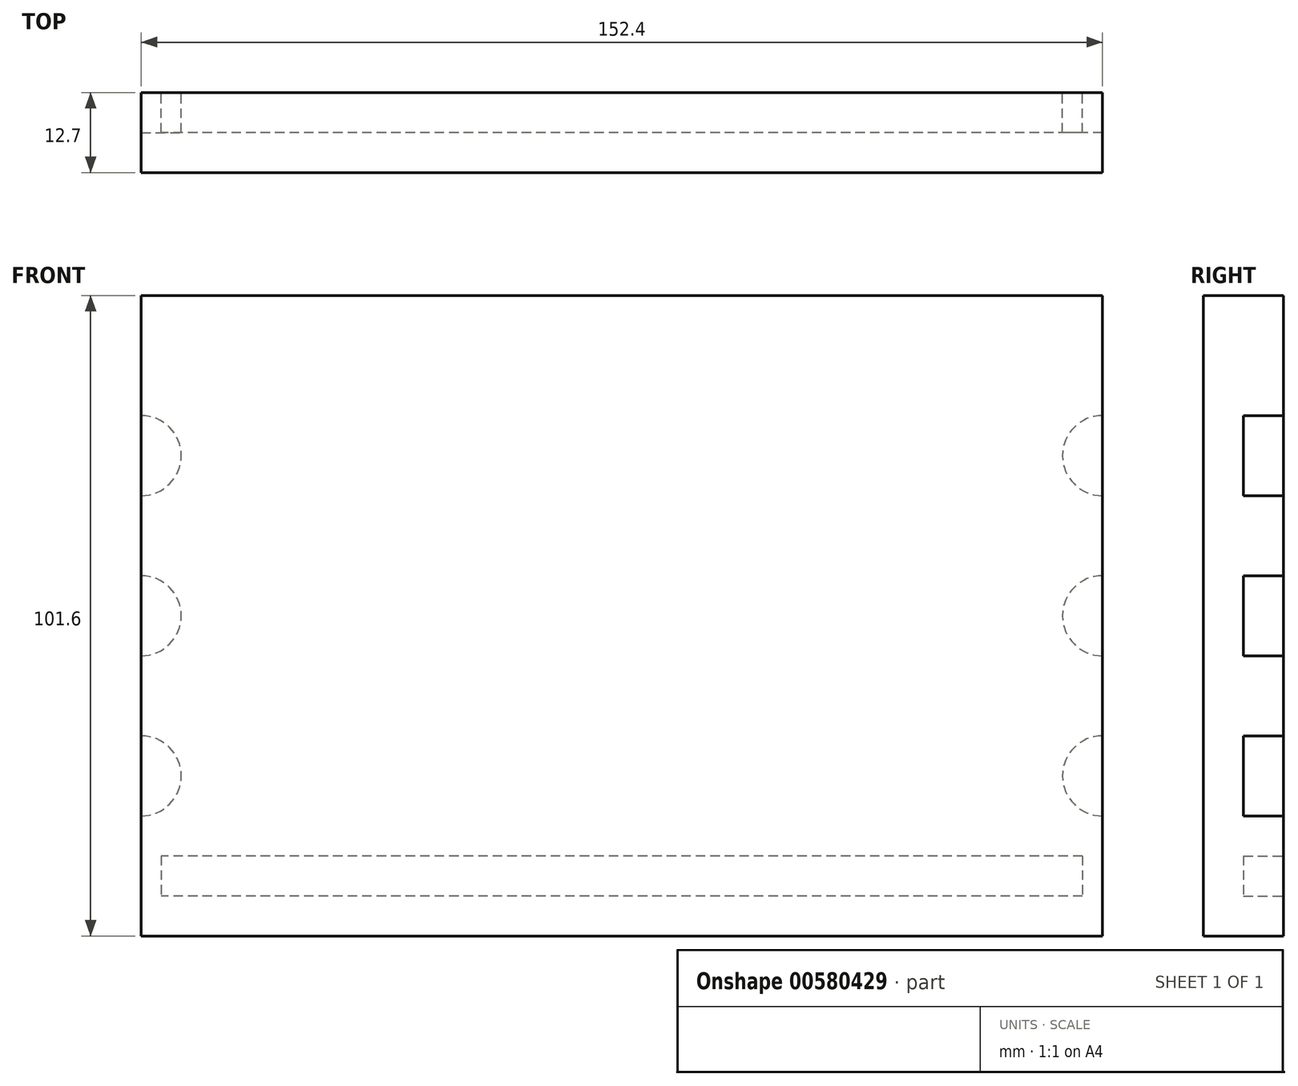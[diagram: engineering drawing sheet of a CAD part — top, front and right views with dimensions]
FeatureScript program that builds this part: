
annotation { "Feature Type Name" : "Feature", "Feature Type Description" : "" }
export const myFeature = defineFeature(function(context is Context, id is Id, definition is map)
    precondition{}
    {
        {
            var Q0;
            Q0=qCreatedBy(makeId("Front.planeOp"),FACE);
            var sketch = newSketch(context, id + "F0", { "sketchPlane" : qUnion([Q0])});
            skLineSegment(sketch, "E0.bottom", {"start": v(76.2, 50.8) * mm, "end": v(-76.2, 50.8) * mm});
            skLineSegment(sketch, "E0.top", {"start": v(76.2, -50.8) * mm, "end": v(-76.2, -50.8) * mm});
            skLineSegment(sketch, "E0.left", {"start": v(76.2, 50.8) * mm, "end": v(76.2, -50.8) * mm});
            skLineSegment(sketch, "E0.right", {"start": v(-76.2, 50.8) * mm, "end": v(-76.2, -50.8) * mm});
            skPoint(sketch, "E0.middle", {"position": v(0, 0) * mm});
            skSolve(sketch);
        }
        {
            var Q0;
            Q0 = qSketchRegion(id + "F0", true);
            var Q1;
            Q1=makeQuery(id+"F0.imprint","IMPRINT",FACE,{"disambiguationData":[TD([[makeQuery(id+"F0.imprint","IMPRINT",EDGE,{"derivedFrom":sQuery(id+"F0.wireOp",EDGE,"E0.bottom")}),1.0]])]});
            extrude(context, id + "F1", {"entities" : qUnion([Q0, Q1]), "depth" : 12.7 * mm, "offsetDistance" : 25.4 * mm});
        }
        {
            var Q0;
            Q0=makeQuery(id+"F1.opExtrude","CAP_FACE",FACE,{"disambiguationData":[OSD([sQuery(id+"F0.wireOp",EDGE,"E0.bottom"),sQuery(id+"F0.wireOp",EDGE,"E0.top"),sQuery(id+"F0.wireOp",EDGE,"E0.left"),sQuery(id+"F0.wireOp",EDGE,"E0.right")])],"isStart":true});
            var sketch = newSketch(context, id + "F2", { "sketchPlane" : qUnion([Q0])});
            skLineSegment(sketch, "E1.bottom", {"start": v(-73.03, -38.1) * mm, "end": v(73.03, -38.1) * mm});
            skLineSegment(sketch, "E1.top", {"start": v(-73.03, -44.45) * mm, "end": v(73.03, -44.45) * mm});
            skLineSegment(sketch, "E1.left", {"start": v(-73.03, -38.1) * mm, "end": v(-73.03, -44.45) * mm});
            skLineSegment(sketch, "E1.right", {"start": v(73.03, -38.1) * mm, "end": v(73.03, -44.45) * mm});
            skSolve(sketch);
        }
        {
            var Q0;
            Q0 = qSketchRegion(id + "F2", true);
            extrude(context, id + "F3", {"entities" : qUnion([Q0]), "operationType" : NewBodyOperationType.REMOVE, "oppositeDirection" : true, "depth" : 6.35 * mm, "offsetDistance" : 25.4 * mm});
        }
        {
            var Q0;
            Q0=makeQuery(id+"F1.opExtrude","CAP_FACE",FACE,{"disambiguationData":[OSD([sQuery(id+"F0.wireOp",EDGE,"E0.bottom"),sQuery(id+"F0.wireOp",EDGE,"E0.top"),sQuery(id+"F0.wireOp",EDGE,"E0.left"),sQuery(id+"F0.wireOp",EDGE,"E0.right")])],"isStart":true});
            var sketch = newSketch(context, id + "F4", { "sketchPlane" : qUnion([Q0])});
            skArc(sketch, "E2", {"start": v(-76.2, 19.05) * mm, "mid": v(-69.85, 25.4) * mm, "end": v(-76.2, 31.75) * mm});
            skArc(sketch, "E3", {"start": v(-76.2, -6.35) * mm, "mid": v(-69.85, 0) * mm, "end": v(-76.2, 6.35) * mm});
            skArc(sketch, "E4", {"start": v(-76.2, -31.75) * mm, "mid": v(-69.85, -25.4) * mm, "end": v(-76.2, -19.05) * mm});
            skArc(sketch, "E5", {"start": v(76.2, 31.75) * mm, "mid": v(69.85, 25.4) * mm, "end": v(76.2, 19.05) * mm});
            skArc(sketch, "E6", {"start": v(76.2, 6.35) * mm, "mid": v(69.85, 0) * mm, "end": v(76.2, -6.35) * mm});
            skArc(sketch, "E7", {"start": v(76.2, -19.05) * mm, "mid": v(69.85, -25.4) * mm, "end": v(76.2, -31.75) * mm});
            skSolve(sketch);
        }
        {
            var Q0;
            {var subQ0=sQuery(id+"F4.wireOp",EDGE,"E5");Q0=makeQuery(id+"F4.imprint","IMPRINT",FACE,{"disambiguationData":[TD([[makeQuery(id+"F4.imprint","IMPRINT",EDGE,{"derivedFrom":subQ0}),1.0]])]});}
            var Q1;
            {var subQ0=sQuery(id+"F4.wireOp",EDGE,"E6");Q1=makeQuery(id+"F4.imprint","IMPRINT",FACE,{"disambiguationData":[TD([[makeQuery(id+"F4.imprint","IMPRINT",EDGE,{"derivedFrom":subQ0}),1.0]])]});}
            var Q2;
            {var subQ0=sQuery(id+"F4.wireOp",EDGE,"E7");Q2=makeQuery(id+"F4.imprint","IMPRINT",FACE,{"disambiguationData":[TD([[makeQuery(id+"F4.imprint","IMPRINT",EDGE,{"derivedFrom":subQ0}),1.0]])]});}
            var Q3;
            {var subQ0=sQuery(id+"F4.wireOp",EDGE,"E4");Q3=makeQuery(id+"F4.imprint","IMPRINT",FACE,{"disambiguationData":[TD([[makeQuery(id+"F4.imprint","IMPRINT",EDGE,{"derivedFrom":subQ0}),1.0]])]});}
            var Q4;
            {var subQ0=sQuery(id+"F4.wireOp",EDGE,"E3");Q4=makeQuery(id+"F4.imprint","IMPRINT",FACE,{"disambiguationData":[TD([[makeQuery(id+"F4.imprint","IMPRINT",EDGE,{"derivedFrom":subQ0}),1.0]])]});}
            var Q5;
            {var subQ0=sQuery(id+"F4.wireOp",EDGE,"E2");Q5=makeQuery(id+"F4.imprint","IMPRINT",FACE,{"disambiguationData":[TD([[makeQuery(id+"F4.imprint","IMPRINT",EDGE,{"derivedFrom":subQ0}),1.0]])]});}
            extrude(context, id + "F5", {"entities" : qUnion([Q0, Q1, Q2, Q3, Q4, Q5]), "operationType" : NewBodyOperationType.REMOVE, "oppositeDirection" : true, "depth" : 6.35 * mm, "offsetDistance" : 25.4 * mm});
        }
    });
